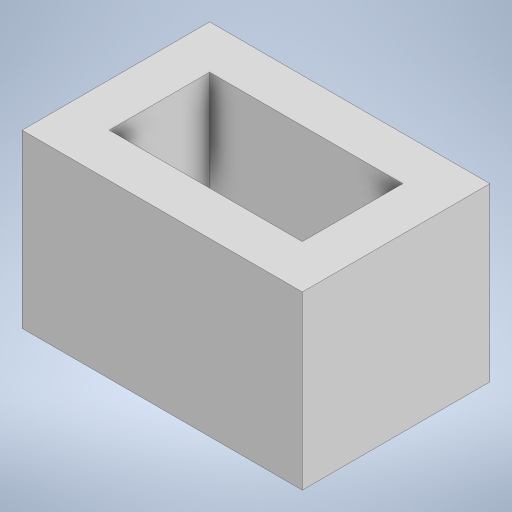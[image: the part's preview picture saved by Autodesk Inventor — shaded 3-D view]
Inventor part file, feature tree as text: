
AUTODESK INVENTOR PART (.ipt)
format: ipt  version: 2023.5 (Build 275446000, 446)  size: 185,344 bytes
history: native  units: in
note: dims shown in document units (in); Inventor stores cm internally (conversion verified against a paired STEP export)
features: extrude x3, sketch x3
ambient origin geometry x8: Origin, YZ Plane, XZ Plane, XY Plane, X Axis, Y Axis, Z Axis, Center Point
bodies: Solid1 (feature_tree)
feature tree (6):
  extrude  "Extrusion1"  Depth=0.2717in
  extrude  "Extrusion2"  Depth=0.1181in
  extrude  "Extrusion3"  Depth=0.1181in
  sketch  "Sketch1"  dims[d0=0.5224in d1=0.2717in]
  sketch  "Sketch2"  dims[d2=0.1181in d3=0.1181in]
  sketch  "Sketch3"  dims[d4=0.1181in d5=0.1181in d6=0.3465in d7=0.0in d8=0.1181in d9=0.0in d10=0.3268in d11=0.1181in d12=0.0in]
